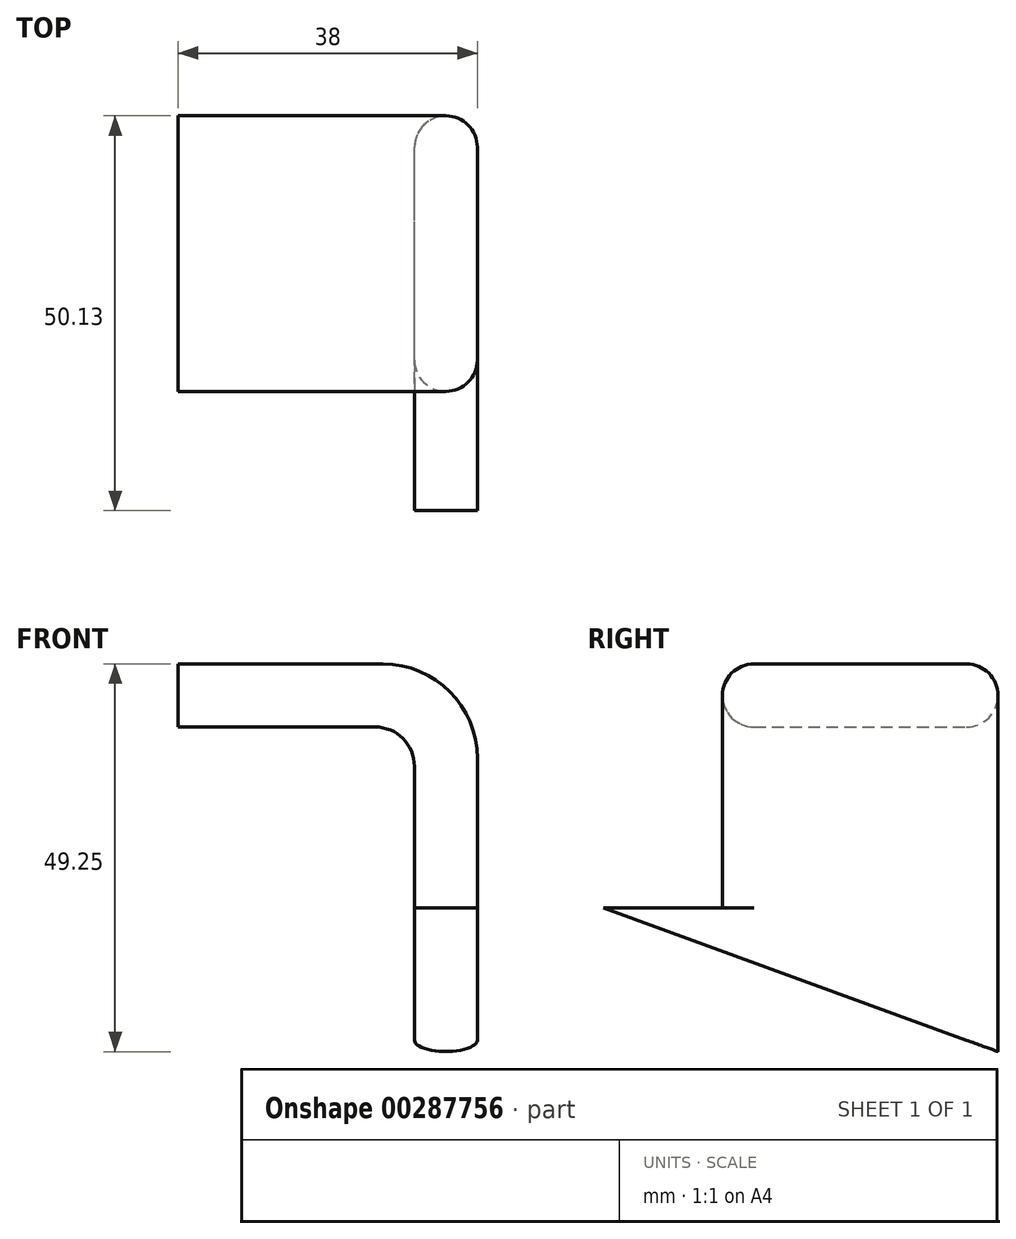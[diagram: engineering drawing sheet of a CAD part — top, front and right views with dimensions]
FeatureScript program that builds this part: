
annotation { "Feature Type Name" : "Feature", "Feature Type Description" : "" }
export const myFeature = defineFeature(function(context is Context, id is Id, definition is map)
    precondition{}
    {
        {
            var Q0;
            Q0=qCreatedBy(makeId("Front.planeOp"),FACE);
            var sketch = newSketch(context, id + "F0", { "sketchPlane" : qUnion([Q0])});
            skLineSegment(sketch, "E0", {"start": v(-30, 23) * mm, "end": v(0, 23) * mm});
            skLineSegment(sketch, "E1", {"start": v(0, 23) * mm, "end": v(0, 0) * mm});
            skLineSegment(sketch, "E2", {"start": v(0, 0) * mm, "end": v(8, 0) * mm});
            skLineSegment(sketch, "E3", {"start": v(8, 0) * mm, "end": v(8, 31) * mm});
            skLineSegment(sketch, "E4", {"start": v(8, 31) * mm, "end": v(-30, 31) * mm});
            skLineSegment(sketch, "E5", {"start": v(-30, 31) * mm, "end": v(-30, 23) * mm});
            skSolve(sketch);
        }
        {
            var Q0;
            Q0=makeQuery(id+"F0.imprint","IMPRINT",FACE,{"disambiguationData":[TD([[makeQuery(id+"F0.imprint","IMPRINT",EDGE,{"derivedFrom":sQuery(id+"F0.wireOp",EDGE,"E0")}),1.0]])]});
            extrude(context, id + "F1", {"entities" : qUnion([Q0]), "depth" : 35 * mm});
        }
        {
            var Q0;
            Q0=qCreatedBy(makeId("Right.planeOp"),FACE);
            var sketch = newSketch(context, id + "F2", { "sketchPlane" : qUnion([Q0])});
            skLineSegment(sketch, "E6", {"start": v(-50.13, 0) * mm, "end": v(0, -18.25) * mm});
            skLineSegment(sketch, "E7", {"start": v(0, -18.25) * mm, "end": v(0, 0) * mm});
            skLineSegment(sketch, "E8", {"start": v(0, 0) * mm, "end": v(-50.13, 0) * mm});
            skSolve(sketch);
        }
        {
            var Q0;
            Q0=makeQuery(id+"F2.imprint","IMPRINT",FACE,{"disambiguationData":[TD([[makeQuery(id+"F2.imprint","IMPRINT",EDGE,{"derivedFrom":sQuery(id+"F2.wireOp",EDGE,"E6")}),1.0]])]});
            extrude(context, id + "F3", {"entities" : qUnion([Q0]), "operationType" : NewBodyOperationType.ADD, "depth" : 8 * mm});
        }
        {
            var Q0;
            Q0=makeQuery(id+"F1.opExtrude","SWEPT_EDGE",EDGE,{"disambiguationData":[OSD([sQuery(id+"F0.wireOp",EDGE,"E0"),sQuery(id+"F0.wireOp",EDGE,"E1")])]});
            fillet(context, id + "F4", {"entities" : qUnion([Q0]), "radius" : 5 * mm, "tangentPropagation" : true, "allowEdgeOverflow" : false});
        }
        {
            var Q0;
            Q0=makeQuery(id+"F1.opExtrude","SWEPT_EDGE",EDGE,{"disambiguationData":[OSD([sQuery(id+"F0.wireOp",EDGE,"E3"),sQuery(id+"F0.wireOp",EDGE,"E4")])]});
            fillet(context, id + "F5", {"entities" : qUnion([Q0]), "radius" : 12 * mm, "tangentPropagation" : true, "allowEdgeOverflow" : false});
        }
        {
            var Q0;
            Q0=makeQuery(id+"F1.opExtrude","CAP_EDGE",EDGE,{"disambiguationData":[OSD([sQuery(id+"F0.wireOp",EDGE,"E4")])],"isStart":false});
            var Q1;
            Q1=makeQuery(id+"F1.opExtrude","CAP_EDGE",EDGE,{"disambiguationData":[OSD([sQuery(id+"F0.wireOp",EDGE,"E0")])],"isStart":false});
            var Q2;
            {var subQ0=sQuery(id+"F0.wireOp",EDGE,"E4");var subQ1=sQuery(id+"F0.wireOp",EDGE,"E3");Q2=makeQuery(id+"F5.opFillet","BLEND_EDGE",EDGE,{"blendedFrom":[makeQuery(id+"F1.opExtrude","SWEPT_EDGE",EDGE,{"disambiguationData":[OSD([subQ1,subQ0])]}),makeQuery(id+"F1.opExtrude","CAP_FACE",FACE,{"disambiguationData":[OSD([sQuery(id+"F0.wireOp",EDGE,"E0"),sQuery(id+"F0.wireOp",EDGE,"E1"),sQuery(id+"F0.wireOp",EDGE,"E2"),subQ1,subQ0,sQuery(id+"F0.wireOp",EDGE,"E5")])],"isStart":false})],"blendedInto":[makeQuery(id+"F1.opExtrude","CAP_FACE",FACE,{"disambiguationData":[OSD([sQuery(id+"F0.wireOp",EDGE,"E0"),sQuery(id+"F0.wireOp",EDGE,"E1"),sQuery(id+"F0.wireOp",EDGE,"E2"),subQ1,subQ0,sQuery(id+"F0.wireOp",EDGE,"E5")])],"isStart":false})]});}
            var Q3;
            {var subQ0=sQuery(id+"F0.wireOp",EDGE,"E1");var subQ1=sQuery(id+"F0.wireOp",EDGE,"E0");Q3=makeQuery(id+"F4.opFillet","BLEND_EDGE",EDGE,{"blendedFrom":[makeQuery(id+"F1.opExtrude","SWEPT_EDGE",EDGE,{"disambiguationData":[OSD([subQ1,subQ0])]}),makeQuery(id+"F1.opExtrude","CAP_FACE",FACE,{"disambiguationData":[OSD([subQ1,subQ0,sQuery(id+"F0.wireOp",EDGE,"E2"),sQuery(id+"F0.wireOp",EDGE,"E3"),sQuery(id+"F0.wireOp",EDGE,"E4"),sQuery(id+"F0.wireOp",EDGE,"E5")])],"isStart":false})],"blendedInto":[makeQuery(id+"F1.opExtrude","CAP_FACE",FACE,{"disambiguationData":[OSD([subQ1,subQ0,sQuery(id+"F0.wireOp",EDGE,"E2"),sQuery(id+"F0.wireOp",EDGE,"E3"),sQuery(id+"F0.wireOp",EDGE,"E4"),sQuery(id+"F0.wireOp",EDGE,"E5")])],"isStart":false})]});}
            var Q4;
            Q4=makeQuery(id+"F1.opExtrude","CAP_EDGE",EDGE,{"disambiguationData":[OSD([sQuery(id+"F0.wireOp",EDGE,"E1")])],"isStart":false});
            var Q5;
            Q5=makeQuery(id+"F1.opExtrude","CAP_EDGE",EDGE,{"disambiguationData":[OSD([sQuery(id+"F0.wireOp",EDGE,"E3")])],"isStart":false});
            fillet(context, id + "F6", {"entities" : qUnion([Q0, Q1, Q2, Q3, Q4, Q5]), "radius" : 4 * mm, "tangentPropagation" : true, "allowEdgeOverflow" : false});
        }
        {
            var Q0;
            Q0=makeQuery(id+"F1.opExtrude","CAP_EDGE",EDGE,{"disambiguationData":[OSD([sQuery(id+"F0.wireOp",EDGE,"E4")])],"isStart":true});
            var Q1;
            Q1=makeQuery(id+"F1.opExtrude","CAP_EDGE",EDGE,{"disambiguationData":[OSD([sQuery(id+"F0.wireOp",EDGE,"E0")])],"isStart":true});
            var Q2;
            Q2=makeQuery(id+"F3.boolean.opBoolean","MERGE",EDGE,{"derivedFrom":[makeQuery(id+"F1.opExtrude","CAP_EDGE",EDGE,{"disambiguationData":[OSD([sQuery(id+"F0.wireOp",EDGE,"E1")])],"isStart":true}),makeQuery(id+"F3.opExtrude","CAP_EDGE",EDGE,{"disambiguationData":[OSD([sQuery(id+"F2.wireOp",EDGE,"E7")])],"isStart":true})]});
            var Q3;
            Q3=makeQuery(id+"F3.boolean.opBoolean","MERGE",EDGE,{"derivedFrom":[makeQuery(id+"F1.opExtrude","CAP_EDGE",EDGE,{"disambiguationData":[OSD([sQuery(id+"F0.wireOp",EDGE,"E3")])],"isStart":true}),makeQuery(id+"F3.opExtrude","CAP_EDGE",EDGE,{"disambiguationData":[OSD([sQuery(id+"F2.wireOp",EDGE,"E7")])],"isStart":false})]});
            var Q4;
            {var subQ0=sQuery(id+"F0.wireOp",EDGE,"E4");var subQ1=sQuery(id+"F0.wireOp",EDGE,"E3");Q4=makeQuery(id+"F5.opFillet","BLEND_EDGE",EDGE,{"blendedFrom":[makeQuery(id+"F1.opExtrude","SWEPT_EDGE",EDGE,{"disambiguationData":[OSD([subQ1,subQ0])]}),makeQuery(id+"F3.boolean.opBoolean","MERGE",FACE,{"derivedFrom":[makeQuery(id+"F1.opExtrude","CAP_FACE",FACE,{"disambiguationData":[OSD([sQuery(id+"F0.wireOp",EDGE,"E0"),sQuery(id+"F0.wireOp",EDGE,"E1"),sQuery(id+"F0.wireOp",EDGE,"E2"),subQ1,subQ0,sQuery(id+"F0.wireOp",EDGE,"E5")])],"isStart":true}),makeQuery(id+"F3.opExtrude","SWEPT_FACE",FACE,{"disambiguationData":[OSD([sQuery(id+"F2.wireOp",EDGE,"E7")])]})]})],"blendedInto":[makeQuery(id+"F3.boolean.opBoolean","MERGE",FACE,{"derivedFrom":[makeQuery(id+"F1.opExtrude","CAP_FACE",FACE,{"disambiguationData":[OSD([sQuery(id+"F0.wireOp",EDGE,"E0"),sQuery(id+"F0.wireOp",EDGE,"E1"),sQuery(id+"F0.wireOp",EDGE,"E2"),subQ1,subQ0,sQuery(id+"F0.wireOp",EDGE,"E5")])],"isStart":true}),makeQuery(id+"F3.opExtrude","SWEPT_FACE",FACE,{"disambiguationData":[OSD([sQuery(id+"F2.wireOp",EDGE,"E7")])]})]})]});}
            var Q5;
            {var subQ0=sQuery(id+"F0.wireOp",EDGE,"E1");var subQ1=sQuery(id+"F0.wireOp",EDGE,"E0");Q5=makeQuery(id+"F4.opFillet","BLEND_EDGE",EDGE,{"blendedFrom":[makeQuery(id+"F1.opExtrude","SWEPT_EDGE",EDGE,{"disambiguationData":[OSD([subQ1,subQ0])]}),makeQuery(id+"F3.boolean.opBoolean","MERGE",FACE,{"derivedFrom":[makeQuery(id+"F1.opExtrude","CAP_FACE",FACE,{"disambiguationData":[OSD([subQ1,subQ0,sQuery(id+"F0.wireOp",EDGE,"E2"),sQuery(id+"F0.wireOp",EDGE,"E3"),sQuery(id+"F0.wireOp",EDGE,"E4"),sQuery(id+"F0.wireOp",EDGE,"E5")])],"isStart":true}),makeQuery(id+"F3.opExtrude","SWEPT_FACE",FACE,{"disambiguationData":[OSD([sQuery(id+"F2.wireOp",EDGE,"E7")])]})]})],"blendedInto":[makeQuery(id+"F3.boolean.opBoolean","MERGE",FACE,{"derivedFrom":[makeQuery(id+"F1.opExtrude","CAP_FACE",FACE,{"disambiguationData":[OSD([subQ1,subQ0,sQuery(id+"F0.wireOp",EDGE,"E2"),sQuery(id+"F0.wireOp",EDGE,"E3"),sQuery(id+"F0.wireOp",EDGE,"E4"),sQuery(id+"F0.wireOp",EDGE,"E5")])],"isStart":true}),makeQuery(id+"F3.opExtrude","SWEPT_FACE",FACE,{"disambiguationData":[OSD([sQuery(id+"F2.wireOp",EDGE,"E7")])]})]})]});}
            fillet(context, id + "F7", {"entities" : qUnion([Q0, Q1, Q2, Q3, Q4, Q5]), "radius" : 4 * mm, "tangentPropagation" : true, "allowEdgeOverflow" : false});
        }
    });
